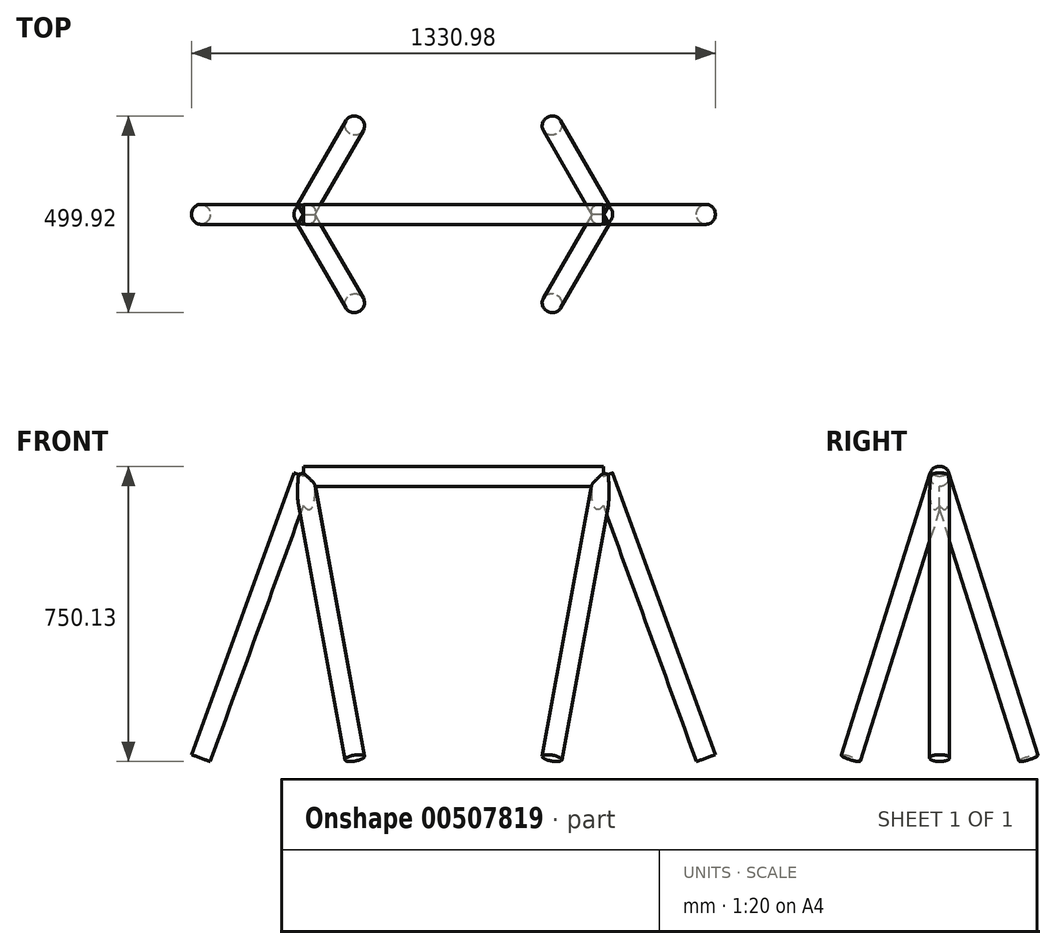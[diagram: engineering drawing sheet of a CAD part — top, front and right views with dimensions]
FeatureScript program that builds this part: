
annotation { "Feature Type Name" : "Feature", "Feature Type Description" : "" }
export const myFeature = defineFeature(function(context is Context, id is Id, definition is map)
    precondition{}
    {
        {
            var Q0;
            Q0=qCreatedBy(makeId("Front.planeOp"),FACE);
            var sketch = newSketch(context, id + "F0", { "sketchPlane" : qUnion([Q0])});
            skLineSegment(sketch, "E0", {"start": v(0, 0) * mm, "end": v(0, 63.23) * mm, "construction": true});
            skLineSegment(sketch, "E1", {"start": v(0, 0) * mm, "end": v(23.87, 8.69) * mm});
            skLineSegment(sketch, "E2", {"start": v(23.87, 8.69) * mm, "end": v(284.49, -707.36) * mm});
            skLineSegment(sketch, "E3", {"start": v(284.49, -707.36) * mm, "end": v(260.62, -716.05) * mm});
            skLineSegment(sketch, "E4", {"start": v(260.62, -716.05) * mm, "end": v(0, 0) * mm});
            skSolve(sketch);
        }
        {
            var Q0;
            Q0=makeQuery(id+"F0.imprint","IMPRINT",FACE,{"disambiguationData":[TD([[makeQuery(id+"F0.imprint","IMPRINT",EDGE,{"derivedFrom":sQuery(id+"F0.wireOp",EDGE,"E1")}),-1.0]])]});
            var Q1;
            Q1=sQuery(id+"F0.wireOp",EDGE,"E4");
            revolve(context, id + "F1", {"entities" : qUnion([Q0]), "axis" : qUnion([Q1]), "revolveType" : RevolveType.FULL});
        }
        {
            var Q0;
            Q0=makeQuery(id+"F1.opRevolve","SWEPT_BODY",BODY,{"disambiguationData":[OSD([sQuery(id+"F0.wireOp",EDGE,"E1"),sQuery(id+"F0.wireOp",EDGE,"E2"),sQuery(id+"F0.wireOp",EDGE,"E3"),sQuery(id+"F0.wireOp",EDGE,"E4")])]});
            var Q1;
            Q1=sQuery(id+"F0.wireOp",EDGE,"E0");
            circularPattern(context, id + "F2", {"operationType" : NewBodyOperationType.ADD, "entities" : qUnion([Q0]), "axis" : qUnion([Q1]), "angle" : 360 * degree, "instanceCount" : 3, "equalSpace" : true});
        }
        {
            var Q0;
            Q0=makeQuery(id+"F1.opRevolve","SWEPT_BODY",BODY,{"disambiguationData":[OSD([sQuery(id+"F0.wireOp",EDGE,"E1"),sQuery(id+"F0.wireOp",EDGE,"E2"),sQuery(id+"F0.wireOp",EDGE,"E3"),sQuery(id+"F0.wireOp",EDGE,"E4")])]});
            transform(context, id + "F3", {"entities" : qUnion([Q0]), "transformType" : TransformType.TRANSLATION_3D, "dx" : -762 * mm, "dy" : 0 * mm, "dz" : 0 * mm, "makeCopy" : true});
        }
        {
            var Q0;
            Q0=qCreatedBy(makeId("Front.planeOp"),FACE);
            var sketch = newSketch(context, id + "F4", { "sketchPlane" : qUnion([Q0])});
            skPoint(sketch, "E5.0", {"position": v(-762, 0) * mm});
            skLineSegment(sketch, "E6", {"start": v(-762, 0) * mm, "end": v(-762, 59.93) * mm, "construction": true});
            skSolve(sketch);
        }
        {
            var Q0;
            Q0=makeQuery(id+"F3.opPattern","COPY",BODY,{"derivedFrom":makeQuery(id+"F1.opRevolve","SWEPT_BODY",BODY,{"disambiguationData":[OSD([sQuery(id+"F0.wireOp",EDGE,"E1"),sQuery(id+"F0.wireOp",EDGE,"E2"),sQuery(id+"F0.wireOp",EDGE,"E3"),sQuery(id+"F0.wireOp",EDGE,"E4")])]}),"instanceName":"1"});
            var Q1;
            Q1=sQuery(id+"F4.wireOp",EDGE,"E6");
            transform(context, id + "F5", {"entities" : qUnion([Q0]), "transformType" : TransformType.ROTATION, "transformAxis" : qUnion([Q1]), "angle" : 180 * degree, "makeCopy" : false});
        }
        {
            var Q0;
            Q0=qCreatedBy(makeId("Front.planeOp"),FACE);
            var sketch = newSketch(context, id + "F6", { "sketchPlane" : qUnion([Q0])});
            skPoint(sketch, "E7.0", {"position": v(-762, 0) * mm});
            skLineSegment(sketch, "E8.bottom", {"start": v(-762, 0) * mm, "end": v(0, 0) * mm});
            skLineSegment(sketch, "E8.top", {"start": v(-762, -25.4) * mm, "end": v(0, -25.4) * mm});
            skLineSegment(sketch, "E8.left", {"start": v(-762, 0) * mm, "end": v(-762, -25.4) * mm});
            skLineSegment(sketch, "E8.right", {"start": v(0, 0) * mm, "end": v(0, -25.4) * mm});
            skSolve(sketch);
        }
        {
            var Q0;
            Q0=makeQuery(id+"F6.imprint","IMPRINT",FACE,{"disambiguationData":[TD([[makeQuery(id+"F6.imprint","IMPRINT",EDGE,{"derivedFrom":sQuery(id+"F6.wireOp",EDGE,"E8.bottom")}),-1.0]])]});
            var Q1;
            Q1=sQuery(id+"F6.wireOp",EDGE,"E8.bottom");
            revolve(context, id + "F7", {"operationType" : NewBodyOperationType.ADD, "entities" : qUnion([Q0]), "axis" : qUnion([Q1]), "revolveType" : RevolveType.FULL});
        }
    });
